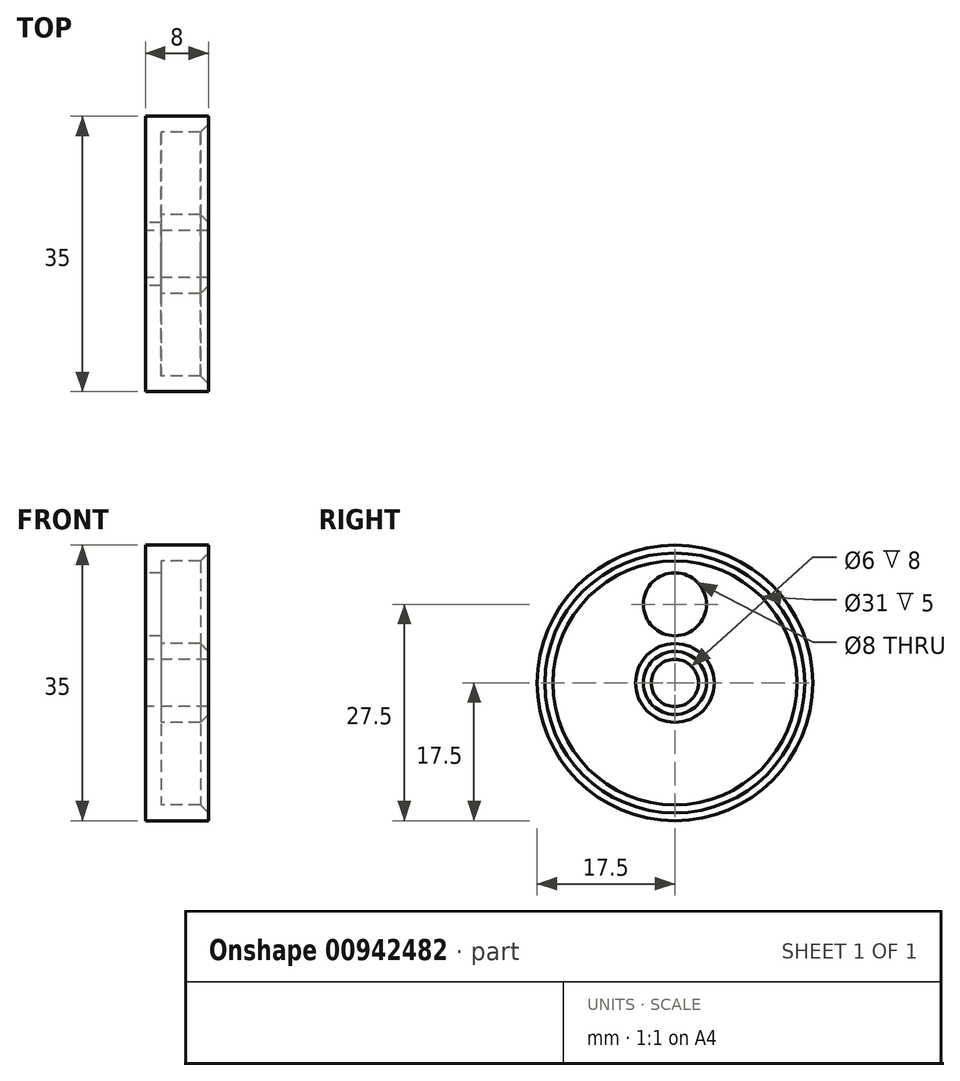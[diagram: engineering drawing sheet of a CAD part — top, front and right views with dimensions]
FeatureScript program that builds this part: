
annotation { "Feature Type Name" : "Feature", "Feature Type Description" : "" }
export const myFeature = defineFeature(function(context is Context, id is Id, definition is map)
    precondition{}
    {
        {
            var Q0;
            Q0=qCreatedBy(makeId("Top.planeOp"),FACE);
            var sketch = newSketch(context, id + "F0", { "sketchPlane" : qUnion([Q0])});
            skLineSegment(sketch, "E0.bottom", {"start": v(0, 0) * mm, "end": v(8, 0) * mm});
            skLineSegment(sketch, "E0.top", {"start": v(0, 17.5) * mm, "end": v(8, 17.5) * mm});
            skLineSegment(sketch, "E0.left", {"start": v(0, 0) * mm, "end": v(0, 17.5) * mm});
            skLineSegment(sketch, "E0.right", {"start": v(8, 0) * mm, "end": v(8, 17.5) * mm});
            skSolve(sketch);
        }
        {
            var Q0;
            Q0=makeQuery(id+"F0.imprint","IMPRINT",FACE,{"disambiguationData":[TD([[makeQuery(id+"F0.imprint","IMPRINT",EDGE,{"derivedFrom":sQuery(id+"F0.wireOp",EDGE,"E0.bottom")}),1.0]])]});
            var Q1;
            Q1=sQuery(id+"F0.wireOp",EDGE,"E0.bottom");
            revolve(context, id + "F1", {"surfaceOperationType" : NewSurfaceOperationType.NEW, "entities" : qUnion([Q0]), "axis" : qUnion([Q1]), "revolveType" : RevolveType.FULL});
        }
        {
            var Q0;
            Q0=qCreatedBy(makeId("Right.planeOp"),FACE);
            var sketch = newSketch(context, id + "F2", { "sketchPlane" : qUnion([Q0])});
            skPoint(sketch, "E1", {"position": v(0, 0) * mm});
            skSolve(sketch);
        }
        {
            var Q0;
            Q0=sQuery(id+"F2.wireOp",VERTEX,"E1");
            var Q1;
            Q1=makeQuery(id+"F1.opRevolve","SWEPT_BODY",BODY,{"disambiguationData":[OSD([sQuery(id+"F0.wireOp",EDGE,"E0.bottom"),sQuery(id+"F0.wireOp",EDGE,"E0.top"),sQuery(id+"F0.wireOp",EDGE,"E0.left"),sQuery(id+"F0.wireOp",EDGE,"E0.right")])]});
            hole(context, id + "F3", {"style" : HoleStyle.SIMPLE, "endStyle" : HoleEndStyle.THROUGH, "oppositeDirection" : true, "holeDiameter" : 6 * mm, "majorDiameter" : 5 * mm, "isTappedThrough" : true, "tappedDepth" : 12 * mm, "tapClearance" : 3, "locations" : qUnion([Q0]), "scope" : qUnion([Q1])});
        }
        {
            var Q0;
            Q0=makeQuery(id+"F1.opRevolve","SWEPT_FACE",FACE,{"disambiguationData":[OSD([sQuery(id+"F0.wireOp",EDGE,"E0.right")])]});
            shell(context, id + "F4", {"entities" : qUnion([Q0]), "thickness" : 2 * mm});
        }
        {
            var Q0;
            Q0=qCreatedBy(makeId("Right.planeOp"),FACE);
            var sketch = newSketch(context, id + "F5", { "sketchPlane" : qUnion([Q0])});
            skPoint(sketch, "E2", {"position": v(0, 10) * mm});
            skSolve(sketch);
        }
        {
            var Q0;
            Q0=sQuery(id+"F5.wireOp",VERTEX,"E2");
            var Q1;
            Q1=makeQuery(id+"F1.opRevolve","SWEPT_BODY",BODY,{"disambiguationData":[OSD([sQuery(id+"F0.wireOp",EDGE,"E0.bottom"),sQuery(id+"F0.wireOp",EDGE,"E0.top"),sQuery(id+"F0.wireOp",EDGE,"E0.left"),sQuery(id+"F0.wireOp",EDGE,"E0.right")])]});
            hole(context, id + "F6", {"style" : HoleStyle.SIMPLE, "endStyle" : HoleEndStyle.THROUGH, "oppositeDirection" : true, "holeDiameter" : 8 * mm, "majorDiameter" : 5 * mm, "isTappedThrough" : true, "tappedDepth" : 12 * mm, "tapClearance" : 3, "locations" : qUnion([Q0]), "scope" : qUnion([Q1])});
        }
        {
            var Q0;
            Q0=makeQuery(id+"F4.opShell","OFFSET_EDGE",EDGE,{"disambiguationData":[OSD([sQuery(id+"F0.wireOp",EDGE,"E0.right"),sQuery(id+"F3.hole-0.sketch.wireOp",EDGE,"core_line_2")])]});
            chamfer(context, id + "F7", {"entities" : qUnion([Q0]), "width" : 1 * mm, "tangentPropagation" : true});
        }
    });
